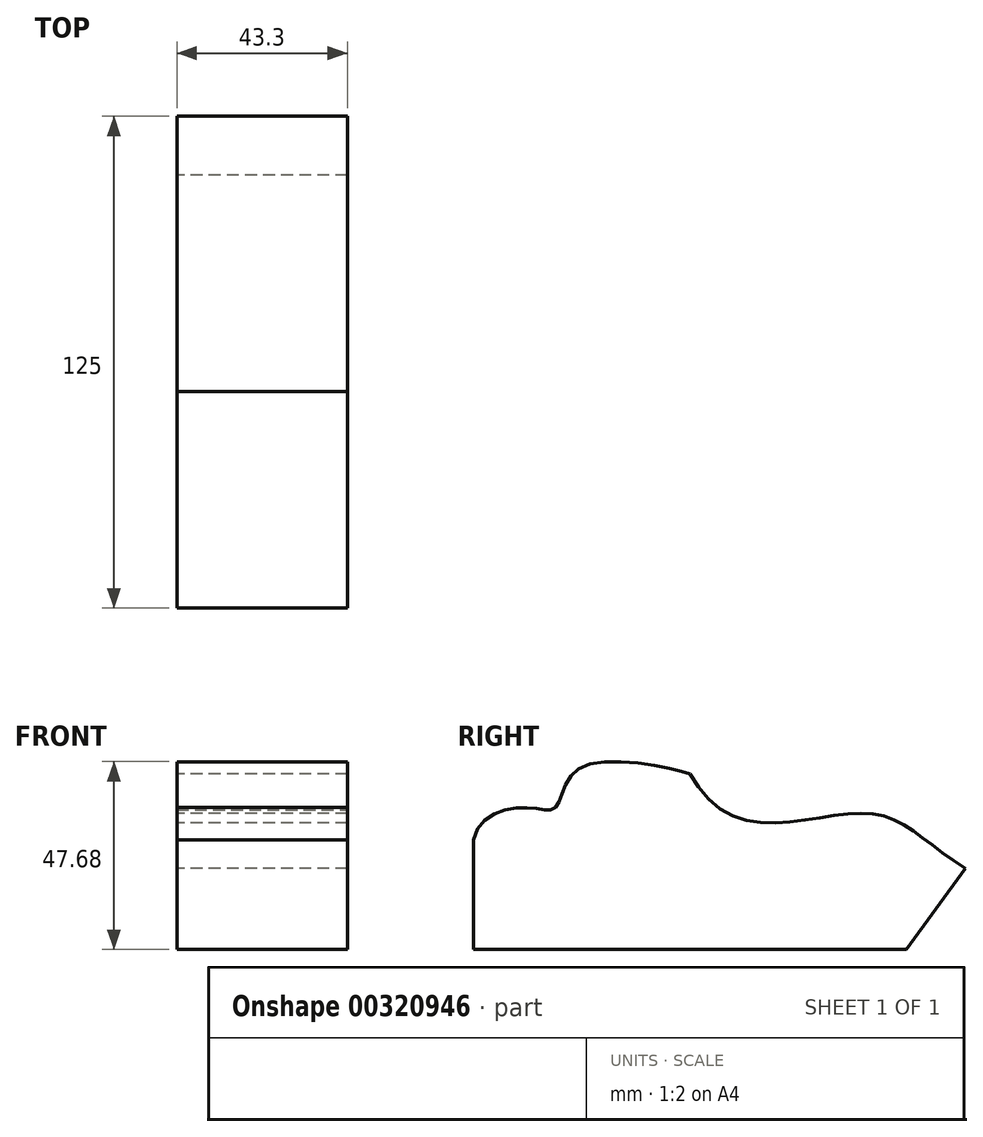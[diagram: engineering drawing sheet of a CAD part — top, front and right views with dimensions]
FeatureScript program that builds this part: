
annotation { "Feature Type Name" : "Feature", "Feature Type Description" : "" }
export const myFeature = defineFeature(function(context is Context, id is Id, definition is map)
    precondition{}
    {
        {
            var Q0;
            Q0=qCreatedBy(makeId("Right.planeOp"),FACE);
            var sketch = newSketch(context, id + "F0", { "sketchPlane" : qUnion([Q0])});
            skLineSegment(sketch, "E0", {"start": v(0, 0) * mm, "end": v(125, 0) * mm});
            skLineSegment(sketch, "E1", {"start": v(125, 0) * mm, "end": v(110, -20.6) * mm});
            skLineSegment(sketch, "E2", {"start": v(110, -20.6) * mm, "end": v(0, -20.6) * mm});
            skLineSegment(sketch, "E3", {"start": v(0, -20.6) * mm, "end": v(0, 15.4) * mm});
            skLineSegment(sketch, "E4", {"start": v(41.7, 25.6) * mm, "end": v(41.7, -20.6) * mm, "construction": true});
            skFitSpline(sketch, "E5", {"points": [v(125, 0) * mm, v(100.86, 13.9) * mm, v(62.5, 15.2) * mm, v(57.69, 36.16) * mm], "startDerivative": vector(-90.35, 54) * mm, "endDerivative": vector(93.94, 3.09) * mm});
            skFitSpline(sketch, "E6", {"points": [v(0, 7.22) * mm, v(13.4, 15.4) * mm, v(20.9, 15.5) * mm, v(27, 25.4) * mm, v(55.1, 24) * mm], "startDerivative": vector(13.24, 72.77) * mm, "endDerivative": vector(37.17, -12.15) * mm});
            skPoint(sketch, "E7", {"position": v(62.5, 0) * mm});
            skSolve(sketch);
        }
        {
            var Q0;
            Q0 = qSketchRegion(id + "F0", true);
            extrude(context, id + "F1", {"entities" : qUnion([Q0]), "depth" : 43.3 * mm});
        }
    });
